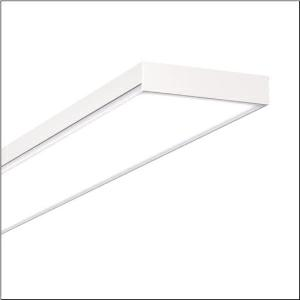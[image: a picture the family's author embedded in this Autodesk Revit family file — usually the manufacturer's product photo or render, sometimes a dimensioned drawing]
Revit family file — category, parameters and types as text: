
# Revit family: apollon_r__31_surface_51mp26wd2441w_24ad
name_source: partatom
category: Lighting Fixtures
units: mm (PartAtom-declared; Revit-internal decimal feet)

## family parameters
Cut with Voids When Loaded = No
Host = Face
Light Source = No
Part Type = Normal
Room Calculation Point = No
Round Connector Dimension = Use Diameter
Shared = No

## types (1)
- Apollon® 31 Surface (1 x LED, 4600 lm, 33 W, 4000K)
    Apparent Load = 33 VA
    CIE Flux Codes = 61 87 97 97 100
    Color Rendering = 80
    Color Temperature = 4000K
    Default Elevation = 1800 mm
    Description = Apollon® 31 Surface, office luminaire, primary optical cover: micro prismatic cover, of PMMA, light emission: direct distribution, primary light characteristic: symmetric, installation type: surface-mounted, LED, rated luminous flux: 4.600lm, luminous efficacy: 139lm/W, light colour: 840, colour temperature: 4000K, control gear: ECG DALI, with terminal, 5-pole, mains connection: 220..240V, AC, 50/60Hz, rated input power: 33W, housing, of sheet steel, coil coated, traffic white (RAL 9016), length: 1.545mm, width: 200mm, height: 44mm, protection rating (complete): IP20, insulation class (complete): insulation class II (safety insulation), certification: CE, impact resistance: IK02, permissible operating ambient temperature: -20..+40°C, standard: EN 60598-2-22, packaging unit: 1 piece
    Height = 44 mm
    Lamp = 1 x LED
    Lamp Light Flux = 4600 lm
    Lamp Power = 33 W
    Lamp count = 1
    Length = 1545 mm
    Luminous efficacy = 139 lm/W
    Manufacturer = Siteco
    ModVariant = No
    Model = 51MP26WD2441W
    Mounting Place = Ceiling
    Mounting Type = Surface mounted
    Number of Poles = 1
    OnlyDefault = Yes
    Power Factor = 1
    Product Name = Apollon® 31 Surface
    Product group = office luminaire | ceiling mounted
    ProductGroupID = 304
    Protection Class = Protection class II
    Protection Degree = IP 20
    RLX_Detail_Level = 1
    RLX_Emergency_Light_Flux = 0 lm
    RLX_Emergency_Type = 0
    RLX_Emergency_Type_DB = No
    RlxData = <blob elided: 20777 chars, md5=d0c22043>
    Socket = socket
    Standby Power = 0 W
    System Light Flux = 4600 lm
    System Power = 33 W
    Type Comments = Product without accessories
    Type Image = l_1007095.jpg
    URL = http://relux.com
    VarID = ---
    Voltage = 0 V
    Weight = 0.00 kg
    Width = 200 mm  [stored 0.656168 ft]

note: [stored X ft] marks values corroborated as IEEE doubles in the binary element streams (Revit-internal decimal feet)

## geometry (parser evidence)
native form markers: Blend x4, Sweep x11
no freeform markers — native parametric forms only
